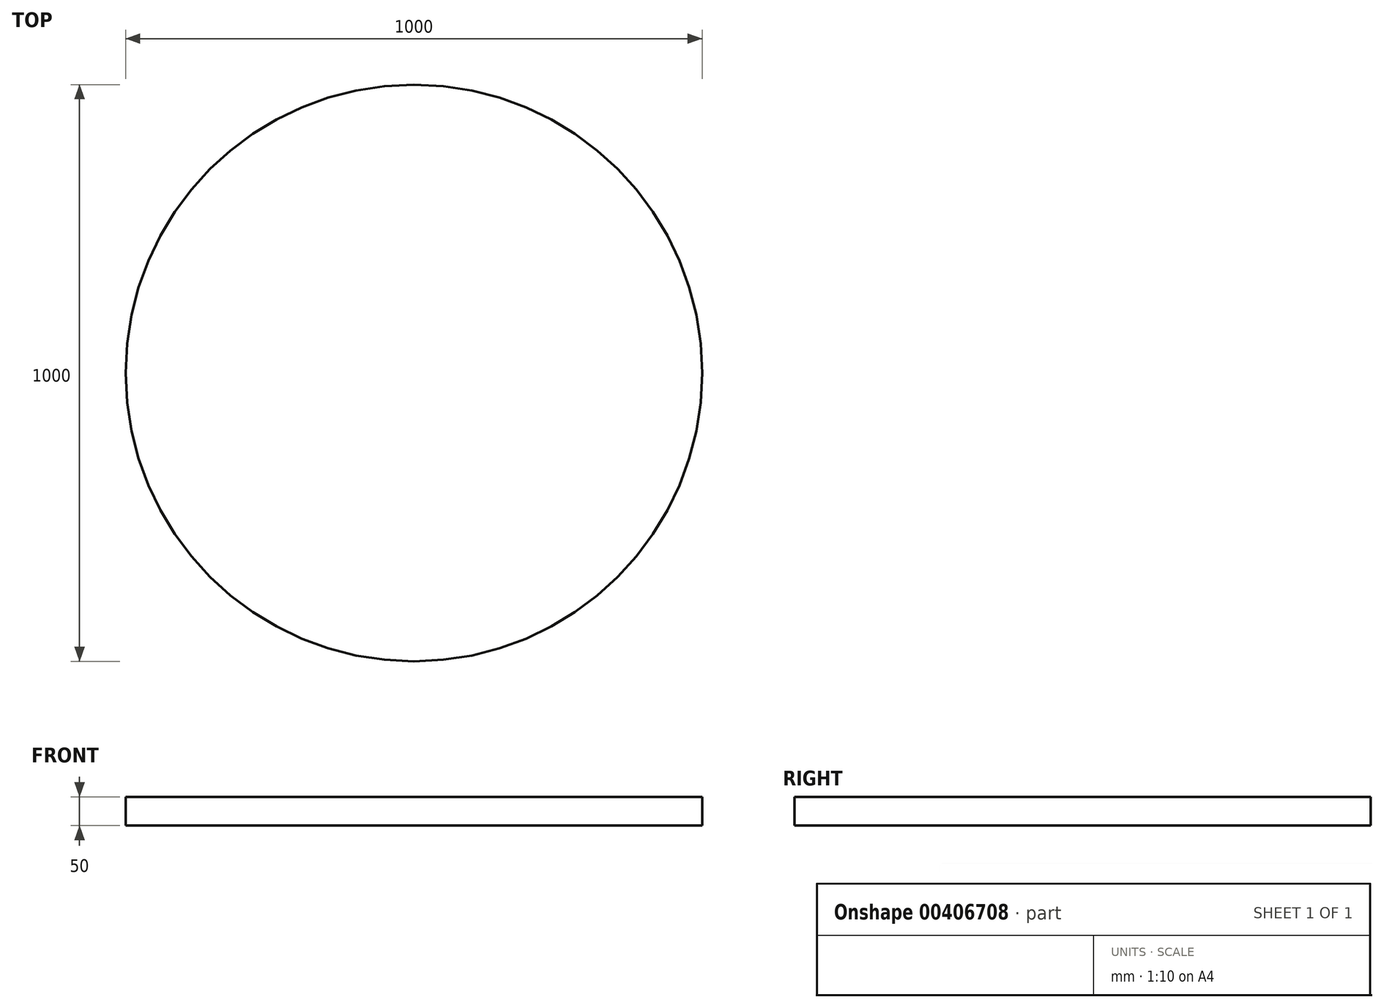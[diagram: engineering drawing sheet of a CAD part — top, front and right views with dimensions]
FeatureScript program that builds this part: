
annotation { "Feature Type Name" : "Feature", "Feature Type Description" : "" }
export const myFeature = defineFeature(function(context is Context, id is Id, definition is map)
    precondition{}
    {
        {
            var Q0;
            Q0=qCreatedBy(makeId("Top.planeOp"),FACE);
            var sketch = newSketch(context, id + "F0", { "sketchPlane" : qUnion([Q0])});
            skCircle(sketch, "E0", {"center": v(0, 0) * mm, "radius": 500 * mm});
            skSolve(sketch);
        }
        {
            var Q0;
            Q0 = qSketchRegion(id + "F0", true);
            extrude(context, id + "F1", {"entities" : qUnion([Q0]), "depth" : 50 * mm});
        }
        {
            var Q0;
            Q0=makeQuery(id+"F1.opExtrude","CAP_FACE",FACE,{"disambiguationData":[OSD([sQuery(id+"F0.wireOp",EDGE,"E0")])],"isStart":false});
            var sketch = newSketch(context, id + "F2", { "sketchPlane" : qUnion([Q0])});
            skLineSegment(sketch, "E1", {"start": v(-283.64, -181.42) * mm, "end": v(-15.3, 336.35) * mm, "construction": true});
            skLineSegment(sketch, "E2", {"start": v(-15.3, 336.35) * mm, "end": v(298.94, -154.93) * mm, "construction": true});
            skLineSegment(sketch, "E3", {"start": v(298.94, -154.93) * mm, "end": v(-283.64, -181.42) * mm, "construction": true});
            skCircle(sketch, "E4", {"center": v(0, 0) * mm, "radius": 336.7 * mm, "construction": true});
            skSolve(sketch);
        }
    });
